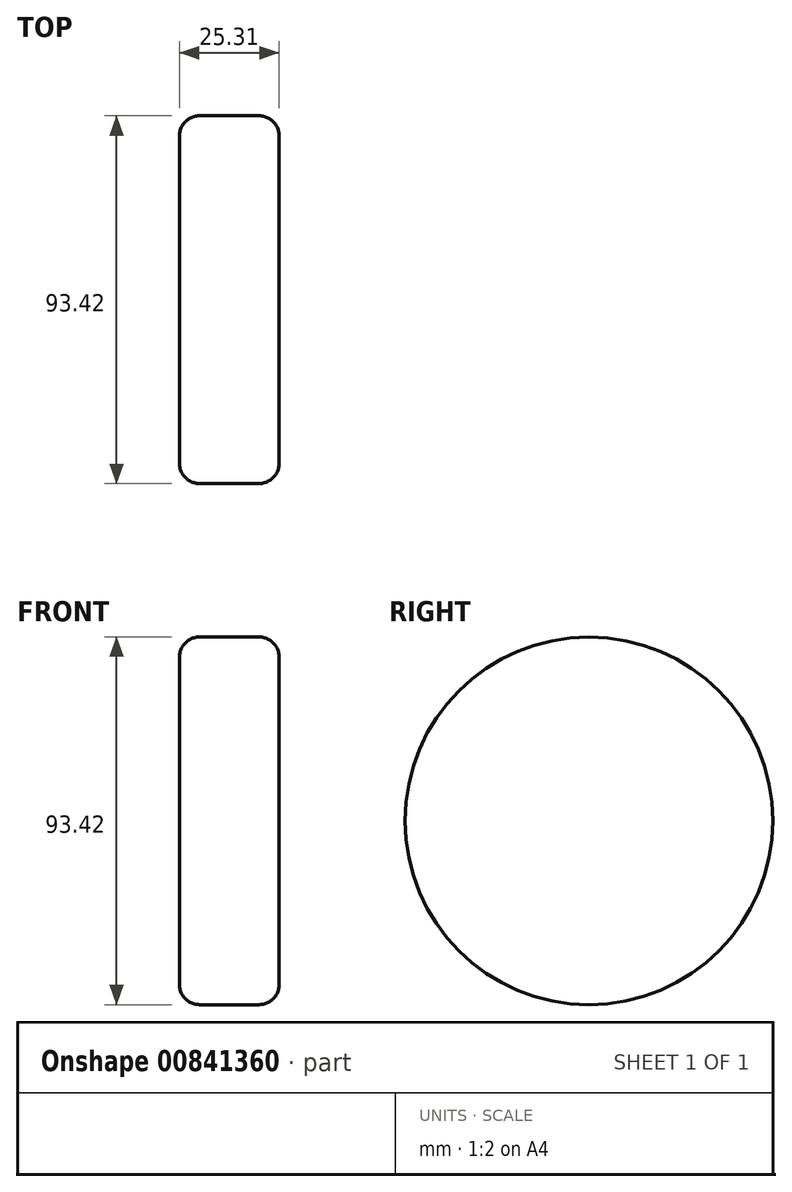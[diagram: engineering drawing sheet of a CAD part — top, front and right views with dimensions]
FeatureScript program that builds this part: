
annotation { "Feature Type Name" : "Feature", "Feature Type Description" : "" }
export const myFeature = defineFeature(function(context is Context, id is Id, definition is map)
    precondition{}
    {
        {
            var Q0;
            Q0=qCreatedBy(makeId("Right.planeOp"),FACE);
            var sketch = newSketch(context, id + "F0", { "sketchPlane" : qUnion([Q0])});
            skCircle(sketch, "E0", {"center": v(0, 0) * mm, "radius": 46.7 * mm});
            skSolve(sketch);
        }
        {
            var Q0;
            Q0=makeQuery(id+"F0.imprint","IMPRINT",FACE,{"disambiguationData":[TD([[makeQuery(id+"F0.imprint","IMPRINT",EDGE,{"derivedFrom":sQuery(id+"F0.wireOp",EDGE,"E0")}),1.0]])]});
            extrude(context, id + "F1", {"entities" : qUnion([Q0]), "depth" : 25.3 * mm, "offsetDistance" : 25.4 * mm});
        }
        {
            var Q0;
            Q0=makeQuery(id+"F1.opExtrude","CAP_EDGE",EDGE,{"disambiguationData":[OSD([sQuery(id+"F0.wireOp",EDGE,"E0")])],"isStart":true});
            var Q1;
            Q1=makeQuery(id+"F1.opExtrude","CAP_EDGE",EDGE,{"disambiguationData":[OSD([sQuery(id+"F0.wireOp",EDGE,"E0")])],"isStart":false});
            fillet(context, id + "F2", {"entities" : qUnion([Q0, Q1]), "radius" : 5.08 * mm, "tangentPropagation" : true, "allowEdgeOverflow" : false});
        }
    });
